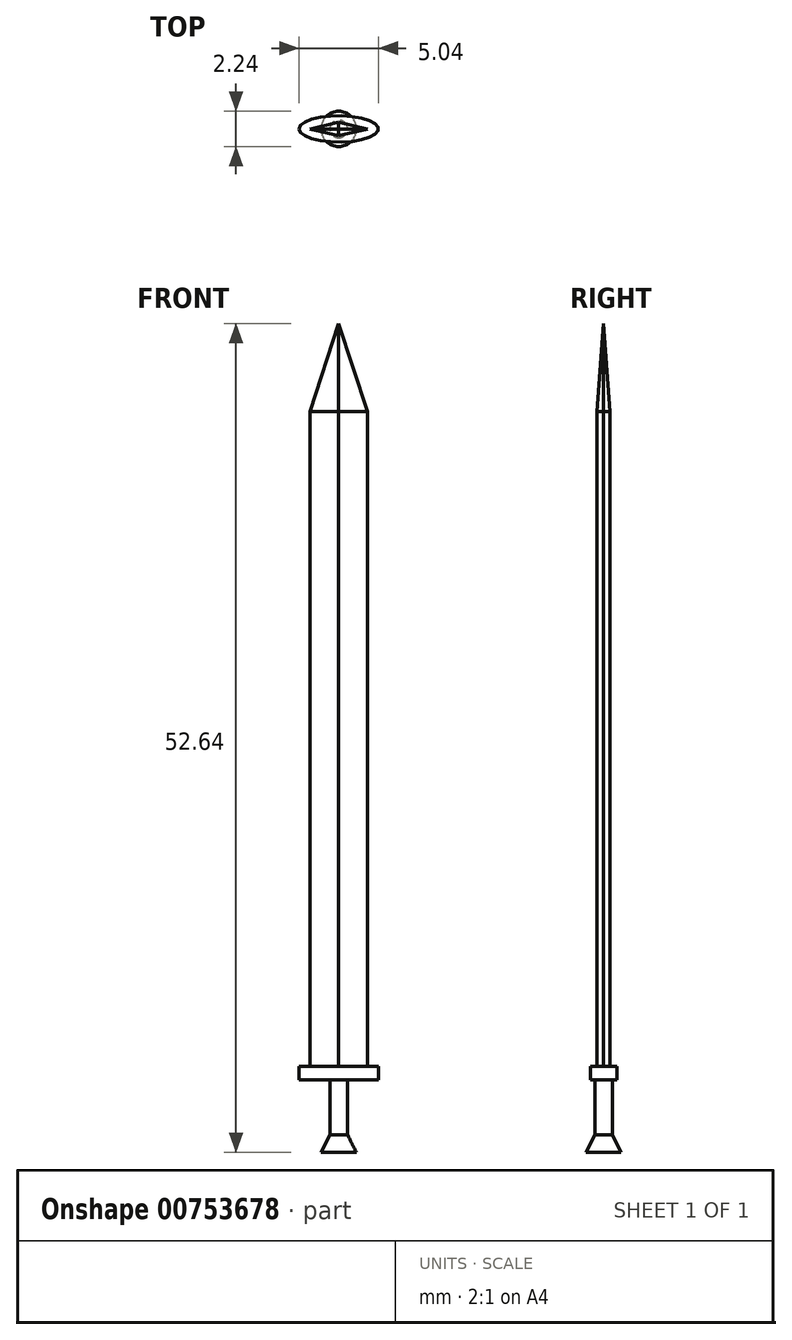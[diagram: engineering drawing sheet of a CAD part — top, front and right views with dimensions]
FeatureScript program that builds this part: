
annotation { "Feature Type Name" : "Feature", "Feature Type Description" : "" }
export const myFeature = defineFeature(function(context is Context, id is Id, definition is map)
    precondition{}
    {
        {
            var Q0;
            Q0=qCreatedBy(makeId("Top.planeOp"),FACE);
            var sketch = newSketch(context, id + "F0", { "sketchPlane" : qUnion([Q0])});
            skCircle(sketch, "E0", {"center": v(12.97, 4.08) * mm, "radius": 0.8 * mm});
            skSolve(sketch);
        }
        {
            var Q0;
            Q0=qCreatedBy(makeId("Top.planeOp"),FACE);
            cPlane(context, id + "F1", {"entities" : qUnion([Q0]), "cplaneType" : CPlaneType.OFFSET, "offset" : 0.8 * mm, "width" : 150 * mm, "height" : 150 * mm});
        }
        {
            var Q0;
            Q0=qCreatedBy(id+"F1.planeOp",FACE);
            var sketch = newSketch(context, id + "F2", { "sketchPlane" : qUnion([Q0])});
            skCircle(sketch, "E1.0", {"center": v(12.97, 4.08) * mm, "radius": 0.8 * mm, "construction": true});
            skCircle(sketch, "E2", {"center": v(12.97, 4.08) * mm, "radius": 0.4 * mm});
            skSolve(sketch);
        }
        {
            var Q0;
            Q0=qCreatedBy(id+"F1.planeOp",FACE);
            cPlane(context, id + "F3", {"entities" : qUnion([Q0]), "cplaneType" : CPlaneType.OFFSET, "offset" : 2.8 * mm, "width" : 150 * mm, "height" : 150 * mm});
        }
        {
            var Q0;
            Q0=qCreatedBy(id+"F3.planeOp",FACE);
            var sketch = newSketch(context, id + "F4", { "sketchPlane" : qUnion([Q0])});
            skCircle(sketch, "E3.0", {"center": v(12.97, 4.08) * mm, "radius": 0.4 * mm, "construction": true});
            skEllipse(sketch, "E4", {"center": v(12.97, 4.08) * mm, "majorRadius": 1.8 * mm, "minorRadius": 0.6 * mm, "majorAxis": v(-1, 0)});
            skSolve(sketch);
        }
        {
            var Q0;
            Q0=makeQuery(id+"F0.imprint","IMPRINT",FACE,{"disambiguationData":[TD([[makeQuery(id+"F0.imprint","IMPRINT",EDGE,{"derivedFrom":sQuery(id+"F0.wireOp",EDGE,"E0")}),1.0]])]});
            var Q1;
            Q1=makeQuery(id+"F2.imprint","IMPRINT",FACE,{"disambiguationData":[TD([[makeQuery(id+"F2.imprint","IMPRINT",EDGE,{"derivedFrom":sQuery(id+"F2.wireOp",EDGE,"E2")}),1.0]])]});
            loft(context, id + "F5", {"sheetProfilesArray" : [{ "sheetProfileEntities" : qUnion([Q0]) }, { "sheetProfileEntities" : qUnion([Q1]) }]});
        }
        {
            var Q0;
            Q0=makeQuery(id+"F5.opLoft","CAP_FACE",FACE,{"disambiguationData":[OSD([makeQuery(id+"F2.imprint","IMPRINT",FACE,{"disambiguationData":[TD([[makeQuery(id+"F2.imprint","IMPRINT",EDGE,{"derivedFrom":sQuery(id+"F2.wireOp",EDGE,"E2")}),1.0]])]})])],"isStart":true});
            extrude(context, id + "F6", {"entities" : qUnion([Q0]), "operationType" : NewBodyOperationType.ADD, "depth" : 2.6 * mm});
        }
        {
            var Q0;
            Q0=makeQuery(id+"F4.imprint","IMPRINT",FACE,{"disambiguationData":[TD([[makeQuery(id+"F4.imprint","IMPRINT",EDGE,{"derivedFrom":sQuery(id+"F4.wireOp",EDGE,"E4")}),1.0]])]});
            extrude(context, id + "F7", {"entities" : qUnion([Q0]), "operationType" : NewBodyOperationType.ADD, "endBound" : BoundingType.SYMMETRIC, "depth" : 0.6 * mm});
        }
        {
            var Q0;
            Q0=qCreatedBy(id+"F3.planeOp",FACE);
            cPlane(context, id + "F8", {"entities" : qUnion([Q0]), "cplaneType" : CPlaneType.OFFSET, "offset" : 0 * mm, "width" : 150 * mm, "height" : 150 * mm});
        }
        {
            var Q0;
            Q0=qCreatedBy(id+"F8.planeOp",FACE);
            var sketch = newSketch(context, id + "F9", { "sketchPlane" : qUnion([Q0])});
            skEllipse(sketch, "E5.0", {"center": v(12.97, 4.08) * mm, "majorRadius": 1.8 * mm, "minorRadius": 0.6 * mm, "majorAxis": v(-1, 0), "construction": true});
            skLineSegment(sketch, "E6", {"start": v(12.97, 5.3) * mm, "end": v(12.97, 2.6) * mm, "construction": true});
            skPoint(sketch, "E6.endSnap0", {"position": v(12.97, 3.48) * mm});
            skLineSegment(sketch, "E7", {"start": v(10.7, 4.08) * mm, "end": v(15.43, 4.08) * mm, "construction": true});
            skPoint(sketch, "E7.startSnap0", {"position": v(11.17, 4.08) * mm});
            skLineSegment(sketch, "E8", {"start": v(11.67, 4.08) * mm, "end": v(12.97, 4.38) * mm});
            skLineSegment(sketch, "E9", {"start": v(12.97, 4.38) * mm, "end": v(14.27, 4.08) * mm});
            skLineSegment(sketch, "E10", {"start": v(14.27, 4.08) * mm, "end": v(12.97, 3.78) * mm});
            skLineSegment(sketch, "E11", {"start": v(12.97, 3.78) * mm, "end": v(11.67, 4.08) * mm});
            skSolve(sketch);
        }
        {
            var Q0;
            Q0=qSketchRegion(id+"F9",true);
            extrude(context, id + "F10", {"entities" : qUnion([Q0]), "operationType" : NewBodyOperationType.ADD, "depth" : 30 * mm});
        }
        {
            var Q0;
            Q0=makeQuery(id+"F10.opExtrude","CAP_FACE",FACE,{"disambiguationData":[OSD([sQuery(id+"F9.wireOp",EDGE,"E8"),sQuery(id+"F9.wireOp",EDGE,"E9"),sQuery(id+"F9.wireOp",EDGE,"E10"),sQuery(id+"F9.wireOp",EDGE,"E11")])],"isStart":false});
            cPlane(context, id + "F11", {"entities" : qUnion([Q0]), "cplaneType" : CPlaneType.OFFSET, "offset" : 4 * mm, "width" : 150 * mm, "height" : 150 * mm});
        }
        {
            var Q0;
            Q0=qCreatedBy(id+"F11.planeOp",FACE);
            var sketch = newSketch(context, id + "F12", { "sketchPlane" : qUnion([Q0])});
            skLineSegment(sketch, "E12.0", {"start": v(12.97, 4.38) * mm, "end": v(14.27, 4.08) * mm, "construction": true});
            skLineSegment(sketch, "E13.0", {"start": v(11.67, 4.08) * mm, "end": v(12.97, 4.38) * mm, "construction": true});
            skLineSegment(sketch, "E14.0", {"start": v(12.97, 3.78) * mm, "end": v(11.67, 4.08) * mm, "construction": true});
            skLineSegment(sketch, "E15.0", {"start": v(14.27, 4.08) * mm, "end": v(12.97, 3.78) * mm, "construction": true});
            skPoint(sketch, "E16", {"position": v(12.97, 4.08) * mm});
            skCircle(sketch, "E17", {"center": v(12.97, 4.08) * mm, "radius": 0 * mm});
            skSolve(sketch);
        }
        {
            var Q1;
            Q1=makeQuery(id+"F10.opExtrude","CAP_FACE",FACE,{"disambiguationData":[OSD([sQuery(id+"F9.wireOp",EDGE,"E8"),sQuery(id+"F9.wireOp",EDGE,"E9"),sQuery(id+"F9.wireOp",EDGE,"E10"),sQuery(id+"F9.wireOp",EDGE,"E11")])],"isStart":false});
            var Q2;
            Q2=sQuery(id+"F12.wireOp",VERTEX,"E16");
            loft(context, id + "F13", {"operationType" : NewBodyOperationType.ADD, "sheetProfilesArray" : [{ "sheetProfileEntities" : qUnion([Q1]) }, { "sheetProfileEntities" : qUnion([Q2]) }]});
        }
        {
            var Q0;
            Q0=makeQuery(id+"F5.opLoft","SWEPT_BODY",BODY,{"disambiguationData":[OSD([makeQuery(id+"F0.imprint","IMPRINT",FACE,{"disambiguationData":[TD([[makeQuery(id+"F0.imprint","IMPRINT",EDGE,{"derivedFrom":sQuery(id+"F0.wireOp",EDGE,"E0")}),1.0]])]}),makeQuery(id+"F2.imprint","IMPRINT",FACE,{"disambiguationData":[TD([[makeQuery(id+"F2.imprint","IMPRINT",EDGE,{"derivedFrom":sQuery(id+"F2.wireOp",EDGE,"E2")}),1.0]])]})])]});
            var Q1;
            Q1=qCreatedBy(makeId("Origin.pointOp"),VERTEX);
            transform(context, id + "F14", {"entities" : qUnion([Q0]), "transformType" : TransformType.SCALE_UNIFORMLY, "scale" : 1.4, "scalePoint" : qUnion([Q1]), "makeCopy" : false});
        }
    });
